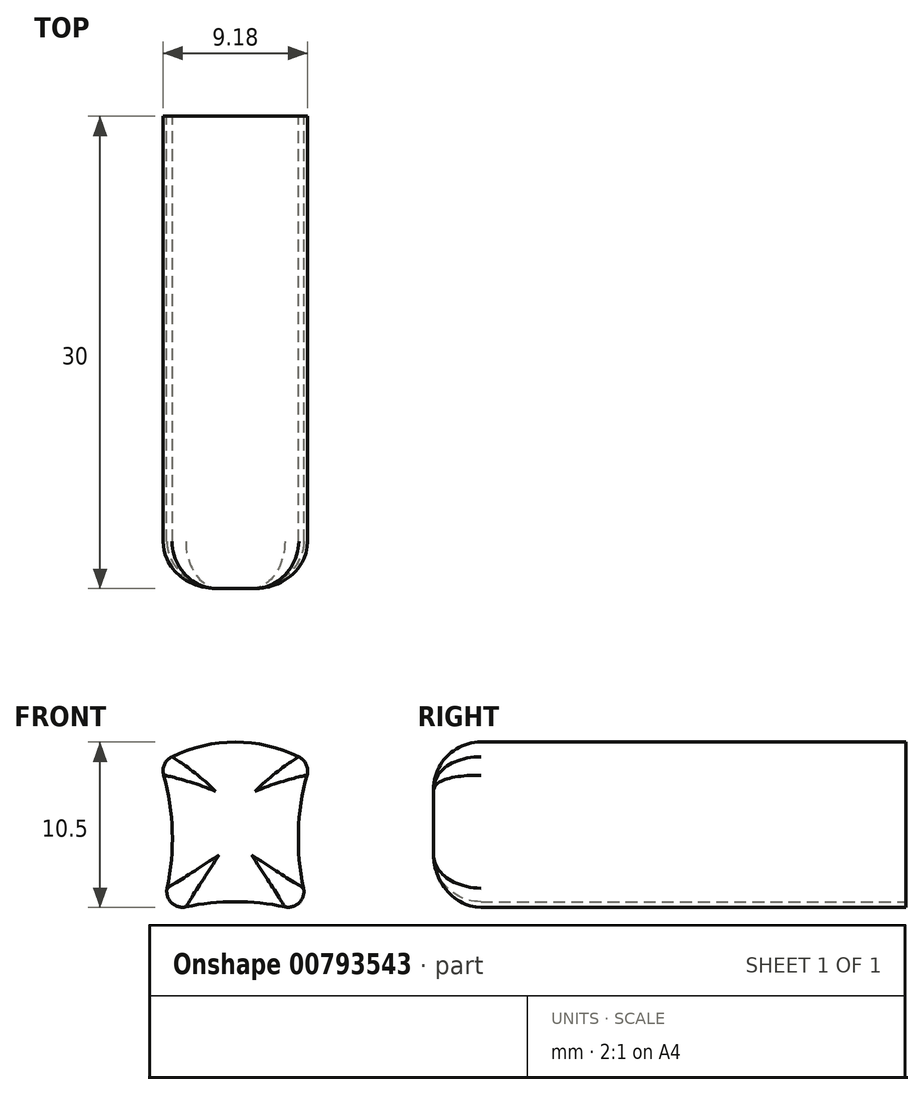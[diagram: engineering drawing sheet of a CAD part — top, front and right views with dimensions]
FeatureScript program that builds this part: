
annotation { "Feature Type Name" : "Feature", "Feature Type Description" : "" }
export const myFeature = defineFeature(function(context is Context, id is Id, definition is map)
    precondition{}
    {
        {
            var Q0;
            Q0=qCreatedBy(makeId("Front.planeOp"),FACE);
            var sketch = newSketch(context, id + "F0", { "sketchPlane" : qUnion([Q0])});
            skPoint(sketch, "E0.middle", {"position": v(0, 0) * mm});
            skArc(sketch, "E1", {"start": v(-4.78, -4.78) * mm, "mid": v(-4, 0) * mm, "end": v(-4.78, 4.78) * mm});
            skLineSegment(sketch, "E2", {"start": v(4.78, -4.78) * mm, "end": v(-4.78, 4.78) * mm, "construction": true});
            skLineSegment(sketch, "E3", {"start": v(4.78, 4.78) * mm, "end": v(-4.78, -4.78) * mm, "construction": true});
            skArc(sketch, "E4.MirrorCS", {"start": v(4.78, 4.78) * mm, "mid": v(4, 0) * mm, "end": v(4.78, -4.78) * mm});
            skArc(sketch, "E5.MirrorCS", {"start": v(-4.78, -4.78) * mm, "mid": v(0, -4) * mm, "end": v(4.78, -4.78) * mm});
            skLineSegment(sketch, "E6", {"start": v(0, 4) * mm, "end": v(0, -4) * mm, "construction": true});
            skArc(sketch, "E7", {"start": v(4.78, 4.78) * mm, "mid": v(0, 6.14) * mm, "end": v(-4.78, 4.78) * mm});
            skSolve(sketch);
        }
        {
            var Q0;
            Q0=qSketchRegion(id+"F0",true);
            extrude(context, id + "F1", {"entities" : qUnion([Q0]), "depth" : 30 * mm, "offsetDistance" : 25 * mm});
        }
        {
            var Q0;
            Q0=makeQuery(id+"F1.opExtrude","CAP_FACE",FACE,{"disambiguationData":[OSD([sQuery(id+"F0.wireOp",EDGE,"E1"),sQuery(id+"F0.wireOp",EDGE,"824459e5-c4f3-42e7-8e47-d3af7f5923630.MirrorCS"),sQuery(id+"F0.wireOp",EDGE,"E4.MirrorCS"),sQuery(id+"F0.wireOp",EDGE,"E5.MirrorCS")])],"isStart":false});
            fillet(context, id + "F2", {"entities" : qUnion([Q0]), "radius" : 3 * mm, "tangentPropagation" : true, "allowEdgeOverflow" : false});
        }
        {
            var Q0;
            Q0=makeQuery(id+"F1.opExtrude","SWEPT_EDGE",EDGE,{"disambiguationData":[OSD([sQuery(id+"F0.wireOp",EDGE,"824459e5-c4f3-42e7-8e47-d3af7f5923630.MirrorCS"),sQuery(id+"F0.wireOp",EDGE,"E4.MirrorCS")])]});
            var Q1;
            Q1=makeQuery(id+"F1.opExtrude","SWEPT_EDGE",EDGE,{"disambiguationData":[OSD([sQuery(id+"F0.wireOp",EDGE,"E1"),sQuery(id+"F0.wireOp",EDGE,"824459e5-c4f3-42e7-8e47-d3af7f5923630.MirrorCS")])]});
            var Q2;
            Q2=makeQuery(id+"F1.opExtrude","SWEPT_EDGE",EDGE,{"disambiguationData":[OSD([sQuery(id+"F0.wireOp",EDGE,"E1"),sQuery(id+"F0.wireOp",EDGE,"E5.MirrorCS")])]});
            var Q3;
            Q3=makeQuery(id+"F1.opExtrude","SWEPT_EDGE",EDGE,{"disambiguationData":[OSD([sQuery(id+"F0.wireOp",EDGE,"E4.MirrorCS"),sQuery(id+"F0.wireOp",EDGE,"E5.MirrorCS")])]});
            fillet(context, id + "F3", {"entities" : qUnion([Q0, Q1, Q2, Q3]), "radius" : 1 * mm, "tangentPropagation" : true, "allowEdgeOverflow" : false});
        }
    });
